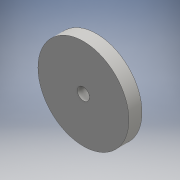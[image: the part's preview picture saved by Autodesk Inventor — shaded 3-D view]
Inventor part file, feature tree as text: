
AUTODESK INVENTOR PART (.ipt)
format: ipt  version: 2016 (Build 200138000, 138)  size: 95,744 bytes
history: native  units: mm
features: extrude x2, sketch x2
ambient origin geometry x8: Origin, YZ Plane, XZ Plane, XY Plane, X Axis, Y Axis, Z Axis, Center Point
bodies: Solid1 (feature_tree)
feature tree (4):
  extrude  "Extrusion1"  Depth=13.0mm TaperAngle=0.0deg
  extrude  "Extrusion2"  Depth=13.0mm TaperAngle=0.0deg
  sketch  "Sketch1"  dims[d0=90.0mm d1=13.0mm d2=0.0mm]
  sketch  "Sketch2"  dims[d3=12.0mm d4=13.0mm d5=0.0mm]
